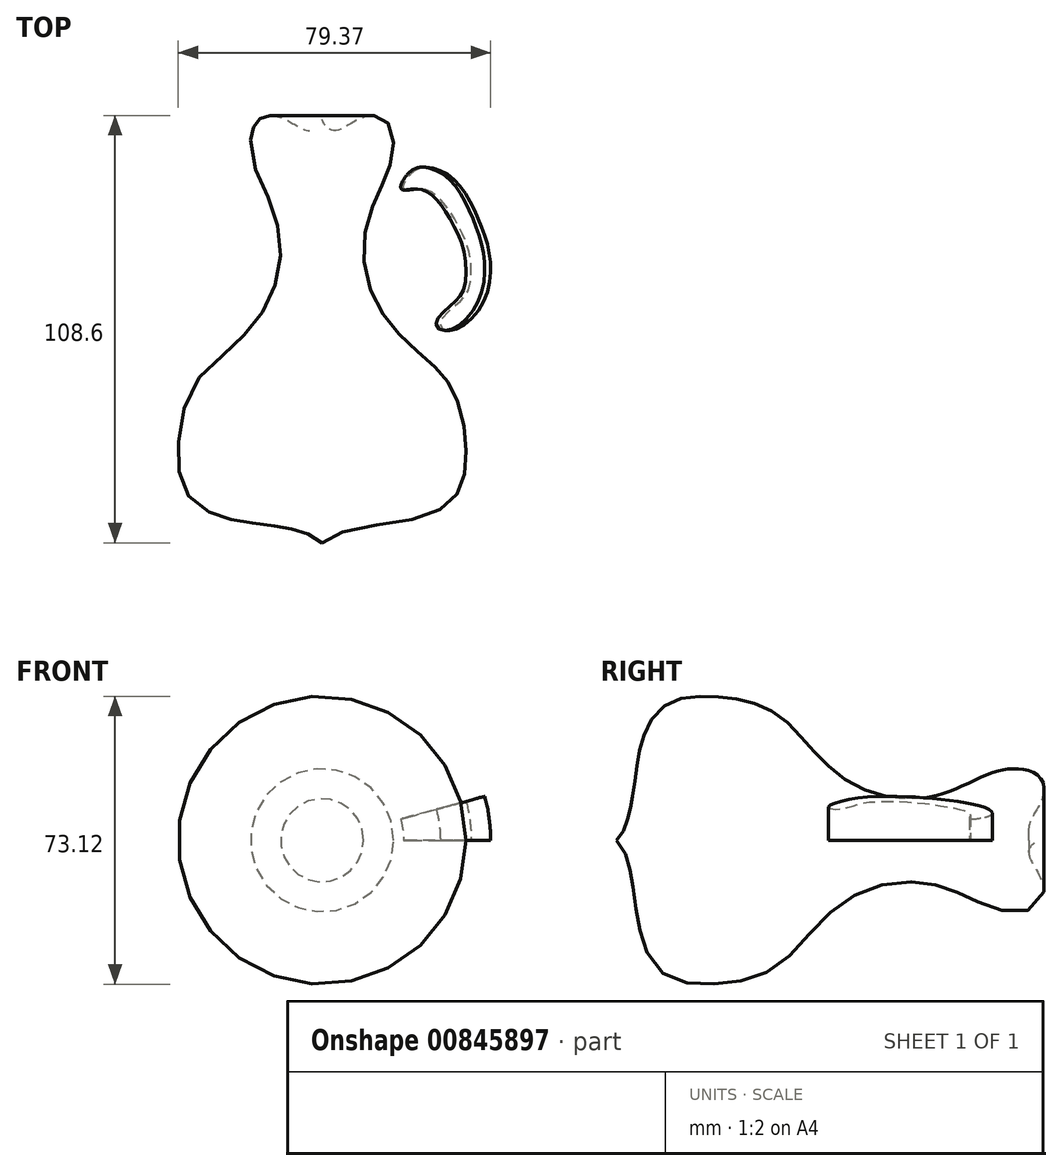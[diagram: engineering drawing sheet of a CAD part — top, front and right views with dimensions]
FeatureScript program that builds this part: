
annotation { "Feature Type Name" : "Feature", "Feature Type Description" : "" }
export const myFeature = defineFeature(function(context is Context, id is Id, definition is map)
    precondition{}
    {
        {
            var Q0;
            Q0=qCreatedBy(makeId("Top.planeOp"),FACE);
            var sketch = newSketch(context, id + "F0", { "sketchPlane" : qUnion([Q0])});
            skLineSegment(sketch, "E0", {"start": v(0, 76.78) * mm, "end": v(0, -75.85) * mm});
            skFitSpline(sketch, "E1", {"points": [v(0, 45) * mm, v(5.27, 47.77) * mm, v(9.7, 49.61) * mm, v(19.5, 48.69) * mm, v(24.11, 38.71) * mm, v(22.45, 30.21) * mm, v(17.65, 16.35) * mm, v(19.86, 2.3) * mm, v(28, -6.74) * mm, v(35.94, -13.95) * mm, v(41.48, -24.3) * mm, v(43.33, -37.97) * mm, v(42.22, -51.46) * mm, v(28.36, -62.92) * mm, v(0, -64.77) * mm, v(4.9, -61.25) * mm, v(25.6, -57.37) * mm, v(34.46, -51.28) * mm, v(36.5, -43.52) * mm, v(35.76, -32.8) * mm, v(32.43, -23.74) * mm, v(27.8, -18.57) * mm, v(20.05, -11.36) * mm, v(13.21, -1.94) * mm, v(10.62, 12.47) * mm, v(13.95, 24.3) * mm, v(17.28, 31.87) * mm, v(17.83, 40.37) * mm, v(14.5, 44.44) * mm, v(8.4, 43.15) * mm, v(2.3, 40.93) * mm, v(0, 45) * mm]});
            skSolve(sketch);
        }
        {
            var Q0;
            {var subQ0=sQuery(id+"F0.wireOp",EDGE,"E1");var subQ1=sQuery(id+"F0.wireOp",EDGE,"E0");var subQ2=makeQuery(id+"F0.imprint","INTERSECT",VERTEX,{"disambiguationData":[OD(0.0)],"derivedFrom":[subQ1,subQ0]});Q0=makeQuery(id+"F0.imprint","IMPRINT",FACE,{"disambiguationData":[TD([[makeQuery(id+"F0.imprint","IMPRINT",EDGE,{"disambiguationData":[TD([[subQ2,-1.0]])],"derivedFrom":subQ1}),1.0]])]});}
            var Q1;
            Q1=sQuery(id+"F0.wireOp",EDGE,"E0");
            revolve(context, id + "F1", {"surfaceOperationType" : NewSurfaceOperationType.NEW, "entities" : qUnion([Q0]), "axis" : qUnion([Q1]), "revolveType" : RevolveType.FULL});
        }
        {
            var Q0;
            Q0=qCreatedBy(makeId("Top.planeOp"),FACE);
            var sketch = newSketch(context, id + "F2", { "sketchPlane" : qUnion([Q0])});
            skFitSpline(sketch, "E2", {"points": [v(22.45, 29.66) * mm, v(26.7, 31.5) * mm, v(33.72, 28.18) * mm, v(39.45, 18.94) * mm, v(42.6, 8.78) * mm, v(40.56, -3.6) * mm, v(32.43, -10.07) * mm, v(30.03, -8.22) * mm, v(33.9, -3.6) * mm, v(37.05, 0) * mm, v(37.6, 8.78) * mm, v(34.65, 16.54) * mm, v(31.14, 22.08) * mm, v(28.18, 24.85) * mm, v(24.48, 25.96) * mm, v(20.79, 25.96) * mm, v(22.45, 29.66) * mm]});
            skLineSegment(sketch, "E3", {"start": v(0, 76.22) * mm, "end": v(0, -75.85) * mm});
            skSolve(sketch);
        }
        {
            var Q0;
            Q0 = qSketchRegion(id + "F2", true);
            var Q1;
            Q1=sQuery(id+"F2.wireOp",EDGE,"E3");
            revolve(context, id + "F3", {"surfaceOperationType" : NewSurfaceOperationType.NEW, "entities" : qUnion([Q0]), "axis" : qUnion([Q1]), "revolveType" : RevolveType.ONE_DIRECTION, "angle" : 15.1 * degree});
        }
    });
